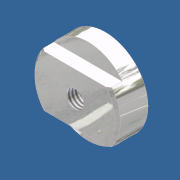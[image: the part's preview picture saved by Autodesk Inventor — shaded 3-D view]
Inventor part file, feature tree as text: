
AUTODESK INVENTOR PART (.ipt)
format: ipt  version: unknown  size: 193,536 bytes
history: native  units: in
note: dims shown in document units (in); Inventor stores cm internally (conversion verified against a paired STEP export)
features: extrude x3, sketch x3, chamfer x1, thread x1
ambient origin geometry x8: Origin, YZ Plane, XZ Plane, XY Plane, X Axis, Y Axis, Z Axis, Center Point
bodies: Solid1 (feature_tree)
feature tree (8):
  extrude  "Extrusion1"  Depth=0.737in TaperAngle=0.0deg
  chamfer  "Chamfer1"  Distance=0.0625in Angle=45.0deg
  extrude  "Extrusion2"  Depth=0.625in
  extrude  "Extrusion3"  Depth=0.425in
  thread  "Thread1"  [1 undecoded]
  sketch  "Sketch1"  dims[d0=2.082in d1=0.737in d2=0.0in d3=0.0625in d4=0.125in d5=45.0deg]
  sketch  "Sketch2"  dims[d6=1.25in d7=0.625in]
  sketch  "Sketch3"  dims[d8=0.32in d9=0.0in d10=0.425in d11=0.32in d12=0.0in d13=1.0in d14=0.0in]
note: 1 required parameter value undecoded (feature->parameter linkage not recoverable at this tier; creation-order binding heuristic only, values carry confidence <= 0.55)
